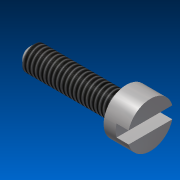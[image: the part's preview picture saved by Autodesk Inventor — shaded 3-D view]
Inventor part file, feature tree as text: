
AUTODESK INVENTOR PART (.ipt)
format: ipt  version: 2015 SP1 (Build 190203100, 203)  size: 109,568 bytes
history: native  units: mm
features: extrude x3, sketch x1, chamfer x1, thread x1, projected_geometry x1
ambient origin geometry x8: Origin, YZ Plane, XZ Plane, XY Plane, X Axis, Y Axis, Z Axis, Center Point
bodies: Solid1 (feature_tree)
feature tree (7):
  sketch  "Sketch1"  dims[d0=4.0mm d1=7.5mm d2=16.0mm d3=0.0mm d4=4.0mm d5=0.0mm d6=2.0mm d7=0.0mm d10=0.8mm d11=2.0mm d12=45.0deg d13=5.0mm d14=0.0mm d15=2.0mm]
  extrude  "Extrusion1"  Depth=2.0mm
  extrude  "Extrusion2"  Depth=16.0mm TaperAngle=0.0deg
  extrude  "Extrusion3"  Depth=4.0mm TaperAngle=0.0deg
  chamfer  "Chamfer1"  Distance=2.0mm
  thread  "Thread2"  [1 undecoded]
  projected_geometry  "Projected Loop1"
note: 1 required parameter value undecoded (feature->parameter linkage not recoverable at this tier; creation-order binding heuristic only, values carry confidence <= 0.55)
